# Revit family: KKDC_MOMO-R_kR030_3000K_1025mm
name_source: partatom
category: 조명 설비
units: mm (PartAtom-declared; Revit-internal decimal feet)

## family parameters
공유 = 아니오
광원 = 예
로드될 때 보이드를 사용하여 절단 = 아니오
룸 계산 점 = 아니오
부품 유형 = 보통
원형 커넥터 치수 = 지름 사용
작업 기준면 기반 = 아니오
주석 방향 유지 = 아니오
항상 수직 = 예

## types (8) — shared parameters
Height = 35
Length = 1025  [stored 3.36286 ft]
Width = 35
감광 램프 색상 온도 변화 = <없음>
경사도 = 90.00°
램프 = kR030
렌더링 시 발산 모양 표시 = 아니오
색상 필터 = 16777215
와티지 해설 = 30W/m
직사각형 길이에서 발산 = 25  [stored 0.082021 ft]
직사각형 폭에서 발산 = 1010  [stored 3.31365 ft]
zero-valued in all types: 기본 높이

## per-type parameters (varying)
| type | 측광 웹 파일 |
| MOMO-R kR030 3000K Clear cover 1025mm | MOMO-R R030 Clear Cover.IES |
| MOMO-R kR030 3000K Clear cover + Micro Louvre 1025mm | MOMO-R R030 Clear Cover+Micro Louvre.IES |
| MOMO-R kR030 3000K Clear cover + 18° (KKLN-01) 1025mm | MOMO-R R030 Clear Cover+18°(KKLN-01).IES |
| MOMO-R kR030 3000K Clear cover + Asymmetric lens (KKLN-A2) 1025mm | MOMO-R R030 Clear Cover+KKLN-A2.IES |
| MOMO-R kR030 3000K Diffused cover 1025mm | MOMO-R R030 Diffused Cover.IES |
| MOMO-R kR030 3000K Clear cover + 23° (KKLN-03) + Micro louvre 1025mm | MOMO-R R030 Clear Cover+23°(KKLN-03)+Micro Louvre.IES |
| MOMO-R kR030 3000K Clear cover + 23° (KKLN-03) 1025mm | MOMO-R R030 Clear Cover+23°(KKLN-03).IES |
| MOMO-R kR030 3000K Clear cover + 18° (KKLN-01) + Micro lovure 1025mm | MOMO-R R030 Clear Cover+18°(KKLN-01)+Micro Louvre.IES |

note: [stored X ft] marks values corroborated as IEEE doubles in the binary element streams (Revit-internal decimal feet)
